# Revit family: lgh-n50_100rkx2(d)_rks2(d)_60Hz
name_source: partatom
category: 機械設備
units: mm (PartAtom-declared; Revit-internal decimal feet)

## family parameters
OmniClass タイトル = Heat Exchangers for Ventilation Air
OmniClass 番号 = 23.75.10.34.21
パーツ タイプ = 標準
ロード時にボイドで切り取り = いいえ
丸型コネクタ寸法 = 直径を使用
作業面ベース = いいえ
共有 = いいえ
常に垂直 = はい
部屋計算ポイント = はい

## types (16) — shared parameters
Box_Depth = 172  [stored 0.564304 ft]
Box_Height = 262  [stored 0.85958 ft]
Box_Width = 115  [stored 0.377297 ft]
Clearance Left = 600
Duct_Depth = 79
EAダクト接続口方向_変更 = いいえ
EAダクト接続口方向_標準 = はい
IfcExportAs = IfcAirToAirHeatRecoveryType
IfcExportType = ROTARYWHEEL
OAダクト接続口方向_変更 = いいえ
OAダクト接続口方向_標準 = はい
OmniClassCode = 23-27 23 19 11
URL = https://www.mitsubishielectric.co.jp
Uniclass2015Code = Pr_60_60_36_88
Uniclass2015Title = Thermal wheels
Uniclass2015Version = Systems v1.9
ドレン管_Depth = 10  [stored 0.0328084 ft]
ドレン管径 = 32 mm
メンテナンススペース = はい
仕様書バージョン = Version1.0
企業コード = 108420
分類コード = 50052504100070
初期抵抗 = 0.0 Pa
加湿給水管径 = 22 mm
周波数 = 60 Hz
呼称 = 全熱交換ユニット
外気量 = 0.0 m³/h
実風量 = 0.0 m³/h
形式 = 天井埋込ダクト形
排気量 = 0.0 m³/h
本体マテリアル = 溶融亜鉛めっき鋼板
法定耐用年数 = 15
消費電力_加湿器 = 0 W
点検口 = はい
点検口1_Depth = 450
点検口1_Width = 450
点検口2_Depth = 450
点検口2_Width = 450
点検口離隔 = 150
相 = 1
積算_科目 = 1 空気調和設備
符号 = HEU
給水管_Depth = 10  [stored 0.0328084 ft]
製品リリース年月 = 2015/1/30
製品出荷対象 = 国内
製造元 = 三菱電機株式会社
設置方法 = 天井吊(隠ぺい)形
設計風量 = 0.0 m³/h
説明 = 業務用ロスナイ 天井埋込形加湿付
負荷分類 = 3_ファン類
運転質量 = 0.00 kg
電動機出力 = 0 W
zero-valued in all types: Clearance Bottom, EAサイズ_W, OAサイズ_W, RAサイズ_W, SAサイズ_W

## per-type parameters (varying)
- LGH-N50RKS2: Box_D=476; Box_H=12  [stored 0.0393701 ft]; Clearance Top=0  [stored 0 ft]; Depth=1288; Duct_Change_Center=124  [stored 0.406824 ft]; Duct_Height=135  [stored 0.442913 ft]; Duct_Height_SA=199  [stored 0.652887 ft]; Duct_Pitch_OA_EA=745; Duct_Pitch_SA_RA=434; Duct_Width_RA=373  [stored 1.22375 ft]; EAサイズ_D=192  [stored 0.629921 ft]; Height=331  [stored 1.08596 ft]; MAX静圧=130.0 Pa; MAX風量=500.0 m³/h; MID静圧=60.0 Pa; MID風量=345.0 m³/h; MIN静圧=13.0 Pa; MIN風量=205.0 m³/h; OAサイズ_D=192  [stored 0.629921 ft]; RAサイズ_D=192  [stored 0.629921 ft]; SAサイズ_D=192  [stored 0.629921 ft]; SMAX静圧=170.0 Pa; SMAX風量=500.0 m³/h; Width=1016; エンタルピ交換効率_冷房=68.00%; エンタルピ交換効率_暖房=68.50%; ドレン管_D=307  [stored 1.00722 ft]; ドレン管_H=25  [stored 0.082021 ft]; 価格=497000 $; 吊りボルト_高さ=85  [stored 0.278871 ft]; 吊りボルトピッチ1=1064; 吊りボルトピッチ2=1275; 天吊金具_幅=20  [stored 0.0656168 ft]; 天吊金具_径=7  [stored 0.0229659 ft]; 有効加湿量=1.4; 極数=2; 機外静圧=170.0 Pa; 機外静圧_排気=170.0 Pa; 消費電力=356 W; 温度交換効率=74.00%; 点検口1_Center=444; 点検口高さ=-331  [stored -1.08596 ft]; 給水管_D=358  [stored 1.17454 ft]; 給水管_H=92  [stored 0.301837 ft]; 製品質量=50.00 kg; 質量=60.00 kg; 電圧=100 V; 面風速=4.4 m/s; 風量=500.0 m³/h; 騒音レベル(dB(A))=35.5
- LGH-N50RKS2D: Box_D=476; Box_H=12  [stored 0.0393701 ft]; Clearance Top=0  [stored 0 ft]; Depth=1288; Duct_Change_Center=124  [stored 0.406824 ft]; Duct_Height=135  [stored 0.442913 ft]; Duct_Height_SA=199  [stored 0.652887 ft]; Duct_Pitch_OA_EA=745; Duct_Pitch_SA_RA=434; Duct_Width_RA=373  [stored 1.22375 ft]; EAサイズ_D=192  [stored 0.629921 ft]; Height=331  [stored 1.08596 ft]; MAX静圧=130.0 Pa; MAX風量=500.0 m³/h; MID静圧=55.0 Pa; MID風量=330.0 m³/h; MIN静圧=10.0 Pa; MIN風量=180.0 m³/h; OAサイズ_D=192  [stored 0.629921 ft]; RAサイズ_D=192  [stored 0.629921 ft]; SAサイズ_D=192  [stored 0.629921 ft]; SMAX静圧=170.0 Pa; SMAX風量=500.0 m³/h; Width=1016; エンタルピ交換効率_冷房=68.00%; エンタルピ交換効率_暖房=68.50%; ドレン管_D=307  [stored 1.00722 ft]; ドレン管_H=25  [stored 0.082021 ft]; 価格=497000 $; 吊りボルト_高さ=85  [stored 0.278871 ft]; 吊りボルトピッチ1=1064; 吊りボルトピッチ2=1275; 天吊金具_幅=20  [stored 0.0656168 ft]; 天吊金具_径=7  [stored 0.0229659 ft]; 有効加湿量=1.4; 極数=3; 機外静圧=170.0 Pa; 機外静圧_排気=170.0 Pa; 消費電力=345 W; 温度交換効率=74.00%; 点検口1_Center=444; 点検口高さ=-331  [stored -1.08596 ft]; 給水管_D=358  [stored 1.17454 ft]; 給水管_H=92  [stored 0.301837 ft]; 製品質量=50.00 kg; 質量=60.00 kg; 電圧=200 V; 面風速=4.4 m/s; 風量=500.0 m³/h; 騒音レベル(dB(A))=35.5
- LGH-N50RKX2: Box_D=476; Box_H=12  [stored 0.0393701 ft]; Clearance Top=0  [stored 0 ft]; Depth=1288; Duct_Change_Center=124  [stored 0.406824 ft]; Duct_Height=135  [stored 0.442913 ft]; Duct_Height_SA=199  [stored 0.652887 ft]; Duct_Pitch_OA_EA=745; Duct_Pitch_SA_RA=434; Duct_Width_RA=373  [stored 1.22375 ft]; EAサイズ_D=192  [stored 0.629921 ft]; Height=331  [stored 1.08596 ft]; MAX静圧=130.0 Pa; MAX風量=500.0 m³/h; MID静圧=60.0 Pa; MID風量=345.0 m³/h; MIN静圧=13.0 Pa; MIN風量=205.0 m³/h; OAサイズ_D=192  [stored 0.629921 ft]; RAサイズ_D=192  [stored 0.629921 ft]; SAサイズ_D=192  [stored 0.629921 ft]; SMAX静圧=170.0 Pa; SMAX風量=500.0 m³/h; Width=1016; エンタルピ交換効率_冷房=68.00%; エンタルピ交換効率_暖房=68.50%; ドレン管_D=307  [stored 1.00722 ft]; ドレン管_H=25  [stored 0.082021 ft]; 価格=704000 $; 参照している仕様書等のバージョン=公共建築工事標準仕様書（機械設備工事編）平成31年度版; 吊りボルト_高さ=85  [stored 0.278871 ft]; 吊りボルトピッチ1=1064; 吊りボルトピッチ2=1275; 天吊金具_幅=20  [stored 0.0656168 ft]; 天吊金具_径=7  [stored 0.0229659 ft]; 有効加湿量=1.4; 極数=2; 機外静圧=170.0 Pa; 機外静圧_排気=170.0 Pa; 消費電力=356 W; 温度交換効率=74.00%; 点検口1_Center=444; 点検口高さ=-331  [stored -1.08596 ft]; 給水管_D=358  [stored 1.17454 ft]; 給水管_H=92  [stored 0.301837 ft]; 製品質量=50.00 kg; 質量=60.00 kg; 電圧=100 V; 面風速=4.4 m/s; 風量=500.0 m³/h; 騒音レベル(dB(A))=35.5
- LGH-N50RKX2D: Box_D=476; Box_H=12  [stored 0.0393701 ft]; Clearance Top=0  [stored 0 ft]; Depth=1288; Duct_Change_Center=124  [stored 0.406824 ft]; Duct_Height=135  [stored 0.442913 ft]; Duct_Height_SA=199  [stored 0.652887 ft]; Duct_Pitch_OA_EA=745; Duct_Pitch_SA_RA=434; Duct_Width_RA=373  [stored 1.22375 ft]; EAサイズ_D=192  [stored 0.629921 ft]; Height=331  [stored 1.08596 ft]; MAX静圧=130.0 Pa; MAX風量=500.0 m³/h; MID静圧=55.0 Pa; MID風量=330.0 m³/h; MIN静圧=10.0 Pa; MIN風量=180.0 m³/h; OAサイズ_D=192  [stored 0.629921 ft]; RAサイズ_D=192  [stored 0.629921 ft]; SAサイズ_D=192  [stored 0.629921 ft]; SMAX静圧=170.0 Pa; SMAX風量=500.0 m³/h; Width=1016; エンタルピ交換効率_冷房=68.00%; エンタルピ交換効率_暖房=68.50%; ドレン管_D=307  [stored 1.00722 ft]; ドレン管_H=25  [stored 0.082021 ft]; 価格=704000 $; 参照している仕様書等のバージョン=公共建築工事標準仕様書（機械設備工事編）平成31年度版; 吊りボルト_高さ=85  [stored 0.278871 ft]; 吊りボルトピッチ1=1064; 吊りボルトピッチ2=1275; 天吊金具_幅=20  [stored 0.0656168 ft]; 天吊金具_径=7  [stored 0.0229659 ft]; 有効加湿量=1.4; 極数=3; 機外静圧=170.0 Pa; 機外静圧_排気=170.0 Pa; 消費電力=345 W; 温度交換効率=74.00%; 点検口1_Center=444; 点検口高さ=-331  [stored -1.08596 ft]; 給水管_D=358  [stored 1.17454 ft]; 給水管_H=92  [stored 0.301837 ft]; 製品質量=50.00 kg; 質量=60.00 kg; 電圧=200 V; 面風速=4.4 m/s; 風量=500.0 m³/h; 騒音レベル(dB(A))=35.5
- LGH-N65RKS2: Box_D=543; Box_H=13; Clearance Top=300; Depth=1390; Duct_Change_Center=124  [stored 0.406824 ft]; Duct_Height=202  [stored 0.66273 ft]; Duct_Height_SA=187  [stored 0.613517 ft]; Duct_Pitch_OA_EA=692; Duct_Pitch_SA_RA=470; Duct_Width_RA=345  [stored 1.13189 ft]; EAサイズ_D=192  [stored 0.629921 ft]; Height=404; MAX静圧=140.0 Pa; MAX風量=650.0 m³/h; MID静圧=90.0 Pa; MID風量=520.0 m³/h; MIN静圧=19.0 Pa; MIN風量=240.0 m³/h; OAサイズ_D=192  [stored 0.629921 ft]; RAサイズ_D=192  [stored 0.629921 ft]; SAサイズ_D=192  [stored 0.629921 ft]; SMAX静圧=195.0 Pa; SMAX風量=650.0 m³/h; Width=954; エンタルピ交換効率_冷房=67.50%; エンタルピ交換効率_暖房=68.50%; ドレン管_D=190; ドレン管_H=23  [stored 0.0754593 ft]; 価格=564000 $; 吊りボルト_高さ=401; 吊りボルトピッチ1=985; 吊りボルトピッチ2=1300; 天吊金具_幅=30  [stored 0.0984252 ft]; 天吊金具_径=7  [stored 0.0229659 ft]; 有効加湿量=1.84; 極数=2; 機外静圧=195.0 Pa; 機外静圧_排気=195.0 Pa; 消費電力=500 W; 温度交換効率=73.00%; 点検口1_Center=454; 点検口高さ=-404  [stored -1.32546 ft]; 給水管_D=385; 給水管_H=159  [stored 0.521654 ft]; 製品質量=68.00 kg; 質量=81.60 kg; 電圧=100 V; 面風速=5.7 m/s; 風量=650.0 m³/h; 騒音レベル(dB(A))=38
- LGH-N65RKS2D: Box_D=543; Box_H=13; Clearance Top=300; Depth=1390; Duct_Change_Center=124  [stored 0.406824 ft]; Duct_Height=202  [stored 0.66273 ft]; Duct_Height_SA=187  [stored 0.613517 ft]; Duct_Pitch_OA_EA=692; Duct_Pitch_SA_RA=470; Duct_Width_RA=345  [stored 1.13189 ft]; EAサイズ_D=192  [stored 0.629921 ft]; Height=404; MAX静圧=140.0 Pa; MAX風量=650.0 m³/h; MID静圧=100.0 Pa; MID風量=550.0 m³/h; MIN静圧=19.0 Pa; MIN風量=240.0 m³/h; OAサイズ_D=192  [stored 0.629921 ft]; RAサイズ_D=192  [stored 0.629921 ft]; SAサイズ_D=192  [stored 0.629921 ft]; SMAX静圧=195.0 Pa; SMAX風量=650.0 m³/h; Width=954; エンタルピ交換効率_冷房=67.50%; エンタルピ交換効率_暖房=68.50%; ドレン管_D=190; ドレン管_H=23  [stored 0.0754593 ft]; 価格=564000 $; 吊りボルト_高さ=401; 吊りボルトピッチ1=985; 吊りボルトピッチ2=1300; 天吊金具_幅=30  [stored 0.0984252 ft]; 天吊金具_径=7  [stored 0.0229659 ft]; 有効加湿量=1.84; 極数=3; 機外静圧=195.0 Pa; 機外静圧_排気=195.0 Pa; 消費電力=505 W; 温度交換効率=73.00%; 点検口1_Center=454; 点検口高さ=-404  [stored -1.32546 ft]; 給水管_D=385; 給水管_H=159  [stored 0.521654 ft]; 製品質量=68.00 kg; 質量=81.60 kg; 電圧=200 V; 面風速=5.7 m/s; 風量=650.0 m³/h; 騒音レベル(dB(A))=38
- LGH-N65RKX2: Box_D=543; Box_H=13; Clearance Top=300; Depth=1390; Duct_Change_Center=124  [stored 0.406824 ft]; Duct_Height=202  [stored 0.66273 ft]; Duct_Height_SA=187  [stored 0.613517 ft]; Duct_Pitch_OA_EA=692; Duct_Pitch_SA_RA=470; Duct_Width_RA=345  [stored 1.13189 ft]; EAサイズ_D=192  [stored 0.629921 ft]; Height=404; MAX静圧=140.0 Pa; MAX風量=650.0 m³/h; MID静圧=90.0 Pa; MID風量=520.0 m³/h; MIN静圧=19.0 Pa; MIN風量=240.0 m³/h; OAサイズ_D=192  [stored 0.629921 ft]; RAサイズ_D=192  [stored 0.629921 ft]; SAサイズ_D=192  [stored 0.629921 ft]; SMAX静圧=195.0 Pa; SMAX風量=650.0 m³/h; Width=954; エンタルピ交換効率_冷房=67.50%; エンタルピ交換効率_暖房=68.50%; ドレン管_D=190; ドレン管_H=23  [stored 0.0754593 ft]; 価格=797000 $; 参照している仕様書等のバージョン=公共建築工事標準仕様書（機械設備工事編）平成31年度版; 吊りボルト_高さ=401; 吊りボルトピッチ1=985; 吊りボルトピッチ2=1300; 天吊金具_幅=30  [stored 0.0984252 ft]; 天吊金具_径=7  [stored 0.0229659 ft]; 有効加湿量=1.84; 極数=2; 機外静圧=195.0 Pa; 機外静圧_排気=195.0 Pa; 消費電力=500 W; 温度交換効率=73.00%; 点検口1_Center=454; 点検口高さ=-404  [stored -1.32546 ft]; 給水管_D=385; 給水管_H=159  [stored 0.521654 ft]; 製品質量=68.00 kg; 質量=81.60 kg; 電圧=100 V; 面風速=5.7 m/s; 風量=650.0 m³/h; 騒音レベル(dB(A))=38
- LGH-N65RKX2D: Box_D=543; Box_H=13; Clearance Top=300; Depth=1390; Duct_Change_Center=124  [stored 0.406824 ft]; Duct_Height=202  [stored 0.66273 ft]; Duct_Height_SA=187  [stored 0.613517 ft]; Duct_Pitch_OA_EA=692; Duct_Pitch_SA_RA=470; Duct_Width_RA=345  [stored 1.13189 ft]; EAサイズ_D=192  [stored 0.629921 ft]; Height=404; MAX静圧=140.0 Pa; MAX風量=650.0 m³/h; MID静圧=100.0 Pa; MID風量=550.0 m³/h; MIN静圧=19.0 Pa; MIN風量=240.0 m³/h; OAサイズ_D=192  [stored 0.629921 ft]; RAサイズ_D=192  [stored 0.629921 ft]; SAサイズ_D=192  [stored 0.629921 ft]; SMAX静圧=195.0 Pa; SMAX風量=650.0 m³/h; Width=954; エンタルピ交換効率_冷房=67.50%; エンタルピ交換効率_暖房=68.50%; ドレン管_D=190; ドレン管_H=23  [stored 0.0754593 ft]; 価格=797000 $; 参照している仕様書等のバージョン=公共建築工事標準仕様書（機械設備工事編）平成31年度版; 吊りボルト_高さ=401; 吊りボルトピッチ1=985; 吊りボルトピッチ2=1300; 天吊金具_幅=30  [stored 0.0984252 ft]; 天吊金具_径=7  [stored 0.0229659 ft]; 有効加湿量=1.84; 極数=3; 機外静圧=195.0 Pa; 機外静圧_排気=195.0 Pa; 消費電力=505 W; 温度交換効率=73.00%; 点検口1_Center=454; 点検口高さ=-404  [stored -1.32546 ft]; 給水管_D=385; 給水管_H=159  [stored 0.521654 ft]; 製品質量=68.00 kg; 質量=81.60 kg; 電圧=200 V; 面風速=5.7 m/s; 風量=650.0 m³/h; 騒音レベル(dB(A))=38
- LGH-N80RKS2: Box_D=571; Box_H=126  [stored 0.413386 ft]; Clearance Top=300; Depth=1572; Duct_Change_Center=165; Duct_Height=202  [stored 0.66273 ft]; Duct_Height_SA=217  [stored 0.711942 ft]; Duct_Pitch_OA_EA=690; Duct_Pitch_SA_RA=400; Duct_Width_RA=345  [stored 1.13189 ft]; EAサイズ_D=242  [stored 0.793963 ft]; Height=404; MAX静圧=115.0 Pa; MAX風量=800.0 m³/h; MID静圧=56.0 Pa; MID風量=560.0 m³/h; MIN静圧=10.0 Pa; MIN風量=240.0 m³/h; OAサイズ_D=242  [stored 0.793963 ft]; RAサイズ_D=242  [stored 0.793963 ft]; SAサイズ_D=242  [stored 0.793963 ft]; SMAX静圧=200.0 Pa; SMAX風量=800.0 m³/h; Width=1004; エンタルピ交換効率_冷房=70.00%; エンタルピ交換効率_暖房=71.00%; ドレン管_D=190; ドレン管_H=23  [stored 0.0754593 ft]; 価格=622000 $; 吊りボルト_高さ=401; 吊りボルトピッチ1=1043; 吊りボルトピッチ2=1465; 天吊金具_幅=30  [stored 0.0984252 ft]; 天吊金具_径=8  [stored 0.0262467 ft]; 有効加湿量=2.21; 極数=2; 機外静圧=200.0 Pa; 機外静圧_排気=200.0 Pa; 消費電力=585 W; 温度交換効率=75.00%; 点検口1_Center=572; 点検口高さ=-404  [stored -1.32546 ft]; 給水管_D=385; 給水管_H=173  [stored 0.567585 ft]; 製品質量=78.00 kg; 質量=93.60 kg; 電圧=100 V; 面風速=4.5 m/s; 風量=800.0 m³/h; 騒音レベル(dB(A))=36
- LGH-N80RKS2D: Box_D=571; Box_H=126  [stored 0.413386 ft]; Clearance Top=300; Depth=1572; Duct_Change_Center=165; Duct_Height=202  [stored 0.66273 ft]; Duct_Height_SA=217  [stored 0.711942 ft]; Duct_Pitch_OA_EA=690; Duct_Pitch_SA_RA=400; Duct_Width_RA=345  [stored 1.13189 ft]; EAサイズ_D=242  [stored 0.793963 ft]; Height=404; MAX静圧=115.0 Pa; MAX風量=800.0 m³/h; MID静圧=38.0 Pa; MID風量=460.0 m³/h; MIN静圧=13.0 Pa; MIN風量=270.0 m³/h; OAサイズ_D=242  [stored 0.793963 ft]; RAサイズ_D=242  [stored 0.793963 ft]; SAサイズ_D=242  [stored 0.793963 ft]; SMAX静圧=200.0 Pa; SMAX風量=800.0 m³/h; Width=1004; エンタルピ交換効率_冷房=70.00%; エンタルピ交換効率_暖房=71.00%; ドレン管_D=190; ドレン管_H=23  [stored 0.0754593 ft]; 価格=622000 $; 吊りボルト_高さ=401; 吊りボルトピッチ1=1043; 吊りボルトピッチ2=1465; 天吊金具_幅=30  [stored 0.0984252 ft]; 天吊金具_径=8  [stored 0.0262467 ft]; 有効加湿量=2.21; 極数=3; 機外静圧=200.0 Pa; 機外静圧_排気=200.0 Pa; 消費電力=625 W; 温度交換効率=75.00%; 点検口1_Center=572; 点検口高さ=-404  [stored -1.32546 ft]; 給水管_D=385; 給水管_H=173  [stored 0.567585 ft]; 製品質量=78.00 kg; 質量=93.60 kg; 電圧=200 V; 面風速=4.5 m/s; 風量=800.0 m³/h; 騒音レベル(dB(A))=36
- LGH-N80RKX2: Box_D=571; Box_H=126  [stored 0.413386 ft]; Clearance Top=300; Depth=1572; Duct_Change_Center=165; Duct_Height=202  [stored 0.66273 ft]; Duct_Height_SA=217  [stored 0.711942 ft]; Duct_Pitch_OA_EA=690; Duct_Pitch_SA_RA=400; Duct_Width_RA=345  [stored 1.13189 ft]; EAサイズ_D=242  [stored 0.793963 ft]; Height=404; MAX静圧=115.0 Pa; MAX風量=800.0 m³/h; MID静圧=56.0 Pa; MID風量=560.0 m³/h; MIN静圧=10.0 Pa; MIN風量=240.0 m³/h; OAサイズ_D=242  [stored 0.793963 ft]; RAサイズ_D=242  [stored 0.793963 ft]; SAサイズ_D=242  [stored 0.793963 ft]; SMAX静圧=200.0 Pa; SMAX風量=800.0 m³/h; Width=1004; エンタルピ交換効率_冷房=70.00%; エンタルピ交換効率_暖房=71.00%; ドレン管_D=190; ドレン管_H=23  [stored 0.0754593 ft]; 価格=882000 $; 参照している仕様書等のバージョン=公共建築工事標準仕様書（機械設備工事編）平成31年度版; 吊りボルト_高さ=401; 吊りボルトピッチ1=1043; 吊りボルトピッチ2=1465; 天吊金具_幅=30  [stored 0.0984252 ft]; 天吊金具_径=8  [stored 0.0262467 ft]; 有効加湿量=2.21; 極数=2; 機外静圧=200.0 Pa; 機外静圧_排気=200.0 Pa; 消費電力=585 W; 温度交換効率=75.00%; 点検口1_Center=572; 点検口高さ=-404  [stored -1.32546 ft]; 給水管_D=385; 給水管_H=173  [stored 0.567585 ft]; 製品質量=78.00 kg; 質量=93.60 kg; 電圧=100 V; 面風速=4.5 m/s; 風量=800.0 m³/h; 騒音レベル(dB(A))=36
- LGH-N80RKX2D: Box_D=571; Box_H=126  [stored 0.413386 ft]; Clearance Top=300; Depth=1572; Duct_Change_Center=165; Duct_Height=202  [stored 0.66273 ft]; Duct_Height_SA=217  [stored 0.711942 ft]; Duct_Pitch_OA_EA=690; Duct_Pitch_SA_RA=400; Duct_Width_RA=345  [stored 1.13189 ft]; EAサイズ_D=242  [stored 0.793963 ft]; Height=404; MAX静圧=115.0 Pa; MAX風量=800.0 m³/h; MID静圧=38.0 Pa; MID風量=460.0 m³/h; MIN静圧=13.0 Pa; MIN風量=270.0 m³/h; OAサイズ_D=242  [stored 0.793963 ft]; RAサイズ_D=242  [stored 0.793963 ft]; SAサイズ_D=242  [stored 0.793963 ft]; SMAX静圧=200.0 Pa; SMAX風量=800.0 m³/h; Width=1004; エンタルピ交換効率_冷房=70.00%; エンタルピ交換効率_暖房=71.00%; ドレン管_D=190; ドレン管_H=23  [stored 0.0754593 ft]; 価格=882000 $; 参照している仕様書等のバージョン=公共建築工事標準仕様書（機械設備工事編）平成31年度版; 吊りボルト_高さ=401; 吊りボルトピッチ1=1043; 吊りボルトピッチ2=1465; 天吊金具_幅=30  [stored 0.0984252 ft]; 天吊金具_径=8  [stored 0.0262467 ft]; 有効加湿量=2.21; 極数=3; 機外静圧=200.0 Pa; 機外静圧_排気=200.0 Pa; 消費電力=625 W; 温度交換効率=75.00%; 点検口1_Center=572; 点検口高さ=-404  [stored -1.32546 ft]; 給水管_D=385; 給水管_H=173  [stored 0.567585 ft]; 製品質量=78.00 kg; 質量=93.60 kg; 電圧=200 V; 面風速=4.5 m/s; 風量=800.0 m³/h; 騒音レベル(dB(A))=36
- LGH-N100RKS2-60: Box_D=571; Box_H=126  [stored 0.413386 ft]; Clearance Top=300; Depth=1572; Duct_Change_Center=165; Duct_Height=162  [stored 0.531496 ft]; Duct_Height_SA=237  [stored 0.777559 ft]; Duct_Pitch_OA_EA=917; Duct_Pitch_SA_RA=560; Duct_Width_RA=459; EAサイズ_D=242  [stored 0.793963 ft]; Height=404; MAX静圧=95.0 Pa; MAX風量=1000.0 m³/h; MID静圧=45.0 Pa; MID風量=670.0 m³/h; MIN静圧=9.0 Pa; MIN風量=300.0 m³/h; OAサイズ_D=242  [stored 0.793963 ft]; RAサイズ_D=242  [stored 0.793963 ft]; SAサイズ_D=242  [stored 0.793963 ft]; SMAX静圧=165.0 Pa; SMAX風量=1000.0 m³/h; Width=1231; エンタルピ交換効率_冷房=70.00%; エンタルピ交換効率_暖房=71.00%; ドレン管_D=190; ドレン管_H=23  [stored 0.0754593 ft]; 価格=755000 $; 吊りボルト_高さ=401; 吊りボルトピッチ1=1270; 吊りボルトピッチ2=1465; 天吊金具_幅=30  [stored 0.0984252 ft]; 天吊金具_径=8  [stored 0.0262467 ft]; 有効加湿量=2.8; 極数=2; 機外静圧=165.0 Pa; 機外静圧_排気=165.0 Pa; 消費電力=720 W; 温度交換効率=75.00%; 点検口1_Center=572; 点検口高さ=-404  [stored -1.32546 ft]; 給水管_D=385; 給水管_H=173  [stored 0.567585 ft]; 製品質量=90.00 kg; 質量=108.00 kg; 電圧=100 V; 面風速=5.7 m/s; 風量=1000.0 m³/h; 騒音レベル(dB(A))=38
- LGH-N100RKS2D-60: Box_D=571; Box_H=126  [stored 0.413386 ft]; Clearance Top=300; Depth=1572; Duct_Change_Center=165; Duct_Height=162  [stored 0.531496 ft]; Duct_Height_SA=237  [stored 0.777559 ft]; Duct_Pitch_OA_EA=917; Duct_Pitch_SA_RA=560; Duct_Width_RA=459; EAサイズ_D=242  [stored 0.793963 ft]; Height=404; MAX静圧=95.0 Pa; MAX風量=1000.0 m³/h; MID静圧=50.0 Pa; MID風量=740.0 m³/h; MIN静圧=10.0 Pa; MIN風量=340.0 m³/h; OAサイズ_D=242  [stored 0.793963 ft]; RAサイズ_D=242  [stored 0.793963 ft]; SAサイズ_D=242  [stored 0.793963 ft]; SMAX静圧=165.0 Pa; SMAX風量=1000.0 m³/h; Width=1231; エンタルピ交換効率_冷房=70.00%; エンタルピ交換効率_暖房=71.00%; ドレン管_D=190; ドレン管_H=23  [stored 0.0754593 ft]; 価格=755000 $; 吊りボルト_高さ=401; 吊りボルトピッチ1=1270; 吊りボルトピッチ2=1465; 天吊金具_幅=30  [stored 0.0984252 ft]; 天吊金具_径=8  [stored 0.0262467 ft]; 有効加湿量=2.8; 極数=3; 機外静圧=165.0 Pa; 機外静圧_排気=165.0 Pa; 消費電力=705 W; 温度交換効率=75.00%; 点検口1_Center=572; 点検口高さ=-404  [stored -1.32546 ft]; 給水管_D=385; 給水管_H=173  [stored 0.567585 ft]; 製品質量=90.00 kg; 質量=108.00 kg; 電圧=200 V; 面風速=5.7 m/s; 風量=1000.0 m³/h; 騒音レベル(dB(A))=38
- LGH-N100RKX2-60: Box_D=571; Box_H=126  [stored 0.413386 ft]; Clearance Top=300; Depth=1572; Duct_Change_Center=165; Duct_Height=162  [stored 0.531496 ft]; Duct_Height_SA=237  [stored 0.777559 ft]; Duct_Pitch_OA_EA=917; Duct_Pitch_SA_RA=560; Duct_Width_RA=459; EAサイズ_D=242  [stored 0.793963 ft]; Height=404; MAX静圧=95.0 Pa; MAX風量=1000.0 m³/h; MID静圧=45.0 Pa; MID風量=670.0 m³/h; MIN静圧=9.0 Pa; MIN風量=300.0 m³/h; OAサイズ_D=242  [stored 0.793963 ft]; RAサイズ_D=242  [stored 0.793963 ft]; SAサイズ_D=242  [stored 0.793963 ft]; SMAX静圧=165.0 Pa; SMAX風量=1000.0 m³/h; Width=1231; エンタルピ交換効率_冷房=70.00%; エンタルピ交換効率_暖房=71.00%; ドレン管_D=190; ドレン管_H=23  [stored 0.0754593 ft]; 価格=1062000 $; 吊りボルト_高さ=401; 吊りボルトピッチ1=1270; 吊りボルトピッチ2=1465; 天吊金具_幅=30  [stored 0.0984252 ft]; 天吊金具_径=8  [stored 0.0262467 ft]; 有効加湿量=2.8; 極数=2; 機外静圧=165.0 Pa; 機外静圧_排気=165.0 Pa; 消費電力=720 W; 温度交換効率=75.00%; 点検口1_Center=572; 点検口高さ=-404  [stored -1.32546 ft]; 給水管_D=385; 給水管_H=173  [stored 0.567585 ft]; 製品質量=90.00 kg; 質量=108.00 kg; 電圧=100 V; 面風速=5.7 m/s; 風量=1000.0 m³/h; 騒音レベル(dB(A))=38
- LGH-N100RKX2D-60: Box_D=571; Box_H=126  [stored 0.413386 ft]; Clearance Top=300; Depth=1572; Duct_Change_Center=165; Duct_Height=162  [stored 0.531496 ft]; Duct_Height_SA=237  [stored 0.777559 ft]; Duct_Pitch_OA_EA=917; Duct_Pitch_SA_RA=560; Duct_Width_RA=459; EAサイズ_D=242  [stored 0.793963 ft]; Height=404; MAX静圧=95.0 Pa; MAX風量=1000.0 m³/h; MID静圧=50.0 Pa; MID風量=740.0 m³/h; MIN静圧=10.0 Pa; MIN風量=340.0 m³/h; OAサイズ_D=242  [stored 0.793963 ft]; RAサイズ_D=242  [stored 0.793963 ft]; SAサイズ_D=242  [stored 0.793963 ft]; SMAX静圧=165.0 Pa; SMAX風量=1000.0 m³/h; Width=1231; エンタルピ交換効率_冷房=70.00%; エンタルピ交換効率_暖房=71.00%; ドレン管_D=190; ドレン管_H=23  [stored 0.0754593 ft]; 価格=1062000 $; 吊りボルト_高さ=401; 吊りボルトピッチ1=1270; 吊りボルトピッチ2=1465; 天吊金具_幅=30  [stored 0.0984252 ft]; 天吊金具_径=8  [stored 0.0262467 ft]; 有効加湿量=2.8; 極数=3; 機外静圧=165.0 Pa; 機外静圧_排気=165.0 Pa; 消費電力=705 W; 温度交換効率=75.00%; 点検口1_Center=572; 点検口高さ=-404  [stored -1.32546 ft]; 給水管_D=385; 給水管_H=173  [stored 0.567585 ft]; 製品質量=90.00 kg; 質量=108.00 kg; 電圧=200 V; 面風速=5.7 m/s; 風量=1000.0 m³/h; 騒音レベル(dB(A))=38

note: column(s) folded — value = type name in every type: モデル

note: [stored X ft] marks values corroborated as IEEE doubles in the binary element streams (Revit-internal decimal feet)

## geometry (parser evidence)
native form markers: Blend x4
no freeform markers — native parametric forms only
